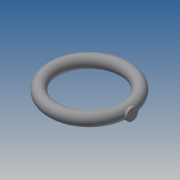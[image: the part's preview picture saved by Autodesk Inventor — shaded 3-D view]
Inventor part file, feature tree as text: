
AUTODESK INVENTOR PART (.ipt)
format: ipt  version: 2014 SP1 (Build 180222100, 222)  size: 129,536 bytes
history: native  units: in
note: dims shown in document units (in); Inventor stores cm internally (conversion verified against a paired STEP export)
features: sketch x2, revolve x1, plane x1, extrude x1
ambient origin geometry x8: Origin, YZ Plane, XZ Plane, XY Plane, X Axis, Y Axis, Z Axis, Center Point
bodies: Solid1 (feature_tree)
feature tree (5):
  revolve  "Revolution1"  [1 undecoded]
  plane  "Work Plane1"
  extrude  "Extrusion1"  Depth=0.1in
  sketch  "Sketch1"  dims[d0=0.25in d1=0.75in]
  sketch  "Sketch2"  dims[d2=90.0deg d3=0.1in d4=0.25in d5=0.05in d6=0.0in]
note: 1 required parameter value undecoded (feature->parameter linkage not recoverable at this tier; creation-order binding heuristic only, values carry confidence <= 0.55)
